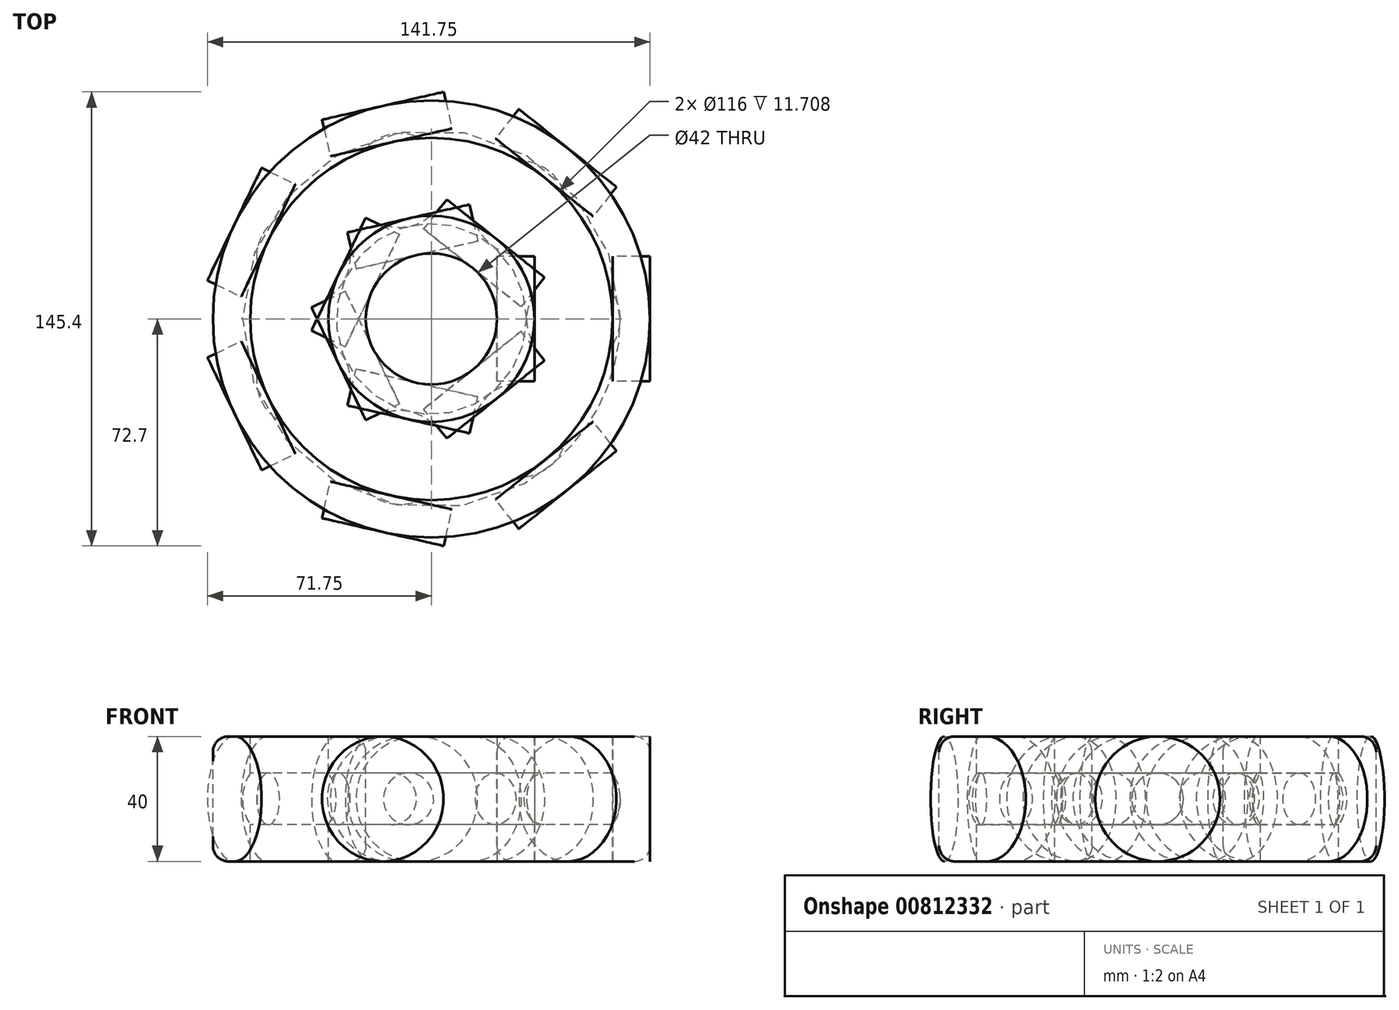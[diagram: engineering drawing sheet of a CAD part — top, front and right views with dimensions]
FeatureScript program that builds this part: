
annotation { "Feature Type Name" : "Feature", "Feature Type Description" : "" }
export const myFeature = defineFeature(function(context is Context, id is Id, definition is map)
    precondition{}
    {
        {
            var Q0;
            Q0=qCreatedBy(makeId("Front.planeOp"),FACE);
            var sketch = newSketch(context, id + "F0", { "sketchPlane" : qUnion([Q0])});
            skLineSegment(sketch, "E0.bottom", {"start": v(21, 20) * mm, "end": v(33, 20) * mm});
            skLineSegment(sketch, "E0.top", {"start": v(21, -20) * mm, "end": v(33, -20) * mm});
            skLineSegment(sketch, "E0.left", {"start": v(21, 20) * mm, "end": v(21, -20) * mm});
            skLineSegment(sketch, "E0.right", {"start": v(33, 20) * mm, "end": v(33, -20) * mm});
            skLineSegment(sketch, "E1.bottom", {"start": v(58, 20) * mm, "end": v(70, 20) * mm});
            skLineSegment(sketch, "E1.top", {"start": v(58, -20) * mm, "end": v(70, -20) * mm});
            skLineSegment(sketch, "E1.left", {"start": v(58, 20) * mm, "end": v(58, -20) * mm});
            skLineSegment(sketch, "E1.right", {"start": v(70, 20) * mm, "end": v(70, -20) * mm});
            skCircle(sketch, "E2", {"center": v(45.5, 0) * mm, "radius": 15 * mm});
            skLineSegment(sketch, "E3", {"start": v(0, 14.76) * mm, "end": v(0, -18.13) * mm});
            skLineSegment(sketch, "E4", {"start": v(0, 0) * mm, "end": v(74.05, 0) * mm});
            skSolve(sketch);
        }
        {
            var Q0;
            {var subQ1=sQuery(id+"F0.wireOp",EDGE,"E0.bottom");Q0=makeQuery(id+"F0.imprint","IMPRINT",FACE,{"disambiguationData":[TD([[makeQuery(id+"F0.imprint","IMPRINT",EDGE,{"derivedFrom":subQ1}),-1.0]])]});}
            var Q1;
            {var subQ4=sQuery(id+"F0.wireOp",EDGE,"E1.bottom");Q1=makeQuery(id+"F0.imprint","IMPRINT",FACE,{"disambiguationData":[TD([[makeQuery(id+"F0.imprint","IMPRINT",EDGE,{"derivedFrom":subQ4}),-1.0]])]});}
            var Q2;
            {var subQ5=sQuery(id+"F0.wireOp",EDGE,"E0.top");Q2=makeQuery(id+"F0.imprint","IMPRINT",FACE,{"disambiguationData":[TD([[makeQuery(id+"F0.imprint","IMPRINT",EDGE,{"derivedFrom":subQ5}),1.0]])]});}
            var Q3;
            {var subQ6=sQuery(id+"F0.wireOp",EDGE,"E1.top");Q3=makeQuery(id+"F0.imprint","IMPRINT",FACE,{"disambiguationData":[TD([[makeQuery(id+"F0.imprint","IMPRINT",EDGE,{"derivedFrom":subQ6}),1.0]])]});}
            var Q4;
            Q4=sQuery(id+"F0.wireOp",EDGE,"E3");
            revolve(context, id + "F1", {"surfaceOperationType" : NewSurfaceOperationType.NEW, "entities" : qUnion([Q0, Q1, Q2, Q3]), "axis" : qUnion([Q4]), "revolveType" : RevolveType.FULL});
        }
        {
            var Q0;
            {var subQ0=sQuery(id+"F0.wireOp",EDGE,"E2");var subQ1=sQuery(id+"F0.wireOp",EDGE,"E0.right");var subQ2=makeQuery(id+"F0.imprint","INTERSECT",VERTEX,{"disambiguationData":[OD(0.0)],"derivedFrom":[subQ1,subQ0]});Q0=makeQuery(id+"F0.imprint","IMPRINT",FACE,{"disambiguationData":[TD([[makeQuery(id+"F0.imprint","IMPRINT",EDGE,{"disambiguationData":[TD([[subQ2,-1.0]])],"derivedFrom":subQ1}),1.0]])]});}
            var Q1;
            {var subQ0=sQuery(id+"F0.wireOp",EDGE,"E2");var subQ1=sQuery(id+"F0.wireOp",EDGE,"E0.right");var subQ2=makeQuery(id+"F0.imprint","INTERSECT",VERTEX,{"disambiguationData":[OD(0.0)],"derivedFrom":[subQ1,subQ0]});Q1=makeQuery(id+"F0.imprint","IMPRINT",FACE,{"disambiguationData":[TD([[makeQuery(id+"F0.imprint","IMPRINT",EDGE,{"disambiguationData":[TD([[subQ2,-1.0]])],"derivedFrom":subQ1}),-1.0]])]});}
            var Q2;
            {var subQ0=sQuery(id+"F0.wireOp",EDGE,"E2");var subQ1=sQuery(id+"F0.wireOp",EDGE,"E1.left");var subQ2=makeQuery(id+"F0.imprint","INTERSECT",VERTEX,{"disambiguationData":[OD(0.0)],"derivedFrom":[subQ1,subQ0]});Q2=makeQuery(id+"F0.imprint","IMPRINT",FACE,{"disambiguationData":[TD([[makeQuery(id+"F0.imprint","IMPRINT",EDGE,{"disambiguationData":[TD([[subQ2,-1.0]])],"derivedFrom":subQ1}),1.0]])]});}
            var Q3;
            Q3=sQuery(id+"F0.wireOp",EDGE,"E4");
            revolve(context, id + "F2", {"surfaceOperationType" : NewSurfaceOperationType.NEW, "entities" : qUnion([Q0, Q1, Q2]), "axis" : qUnion([Q3]), "revolveType" : RevolveType.FULL});
        }
        {
            var Q0;
            Q0=makeQuery(id+"F1.opRevolve","SWEPT_EDGE",EDGE,{"disambiguationData":[OSD([sQuery(id+"F0.wireOp",EDGE,"E0.bottom"),sQuery(id+"F0.wireOp",EDGE,"E0.left")])]});
            var Q1;
            Q1=makeQuery(id+"F1.opRevolve","SWEPT_EDGE",EDGE,{"disambiguationData":[OSD([sQuery(id+"F0.wireOp",EDGE,"E1.bottom"),sQuery(id+"F0.wireOp",EDGE,"E1.right")])]});
            var Q2;
            Q2=makeQuery(id+"F1.opRevolve","SWEPT_EDGE",EDGE,{"disambiguationData":[OSD([sQuery(id+"F0.wireOp",EDGE,"E0.top"),sQuery(id+"F0.wireOp",EDGE,"E0.left")])]});
            var Q3;
            Q3=makeQuery(id+"F1.opRevolve","SWEPT_EDGE",EDGE,{"disambiguationData":[OSD([sQuery(id+"F0.wireOp",EDGE,"E1.top"),sQuery(id+"F0.wireOp",EDGE,"E1.right")])]});
            fillet(context, id + "F3", {"entities" : qUnion([Q0, Q1, Q2, Q3]), "radius" : 5 * mm, "tangentPropagation" : true, "allowEdgeOverflow" : false});
        }
        {
            var Q0;
            Q0=makeQuery(id+"F2.opRevolve","SWEPT_BODY",BODY,{"disambiguationData":[OSD([sQuery(id+"F0.wireOp",EDGE,"E2"),sQuery(id+"F0.wireOp",EDGE,"E4")])]});
            var Q1;
            Q1=makeQuery(id+"F1.opRevolve","SWEPT_FACE",FACE,{"disambiguationData":[OSD([sQuery(id+"F0.wireOp",EDGE,"E0.left")])]});
            circularPattern(context, id + "F4", {"entities" : qUnion([Q0]), "axis" : qUnion([Q1]), "angle" : 360 * degree, "instanceCount" : 7, "equalSpace" : true});
        }
    });
